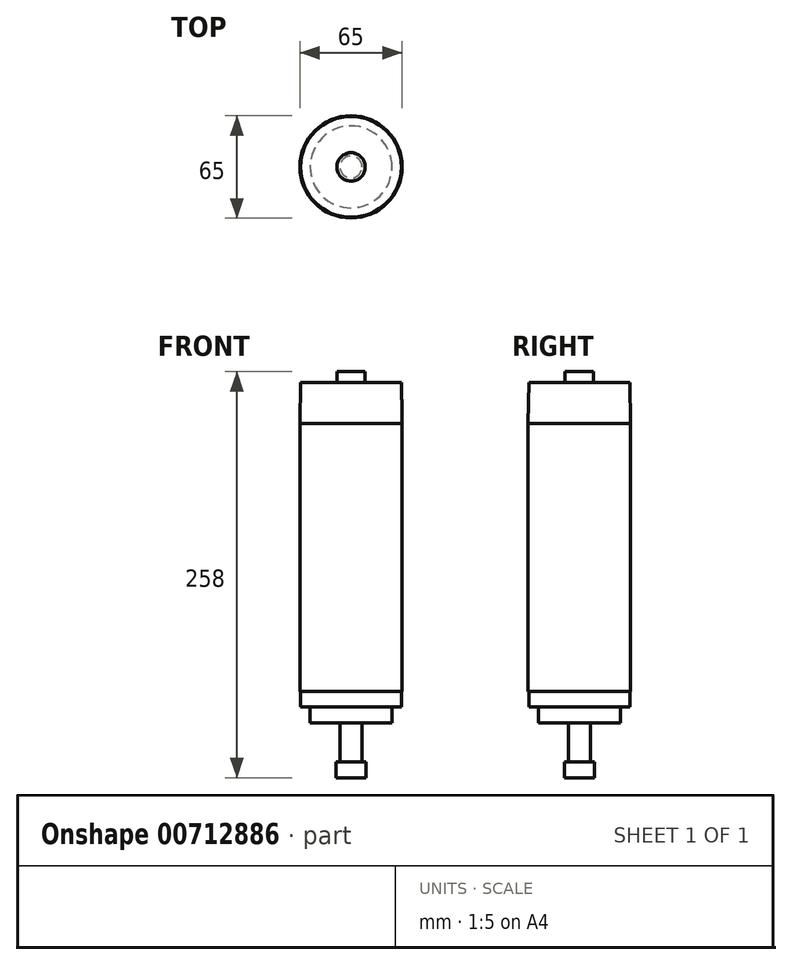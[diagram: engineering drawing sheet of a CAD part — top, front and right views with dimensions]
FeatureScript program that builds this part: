
annotation { "Feature Type Name" : "Feature", "Feature Type Description" : "" }
export const myFeature = defineFeature(function(context is Context, id is Id, definition is map)
    precondition{}
    {
        {
            var Q0;
            Q0=qCreatedBy(makeId("Top.planeOp"),FACE);
            var sketch = newSketch(context, id + "F0", { "sketchPlane" : qUnion([Q0])});
            skCircle(sketch, "E0", {"center": v(0, 0) * mm, "radius": 32.5 * mm});
            skSolve(sketch);
        }
        {
            var Q0;
            Q0 = qSketchRegion(id + "F0", true);
            extrude(context, id + "F1", {"entities" : qUnion([Q0]), "depth" : (170 + 26) * mm, "offsetDistance" : 25 * mm});
        }
        {
            var Q0;
            Q0=makeQuery(id+"F1.opExtrude","CAP_EDGE",EDGE,{"disambiguationData":[OSD([sQuery(id+"F0.wireOp",EDGE,"E0")])],"isStart":false});
            chamfer(context, id + "F2", {"entities" : qUnion([Q0]), "chamferType" : ChamferType.TWO_OFFSETS, "width1" : 26 * mm, "oppositeDirection" : true, "width2" : 0.5 * mm, "tangentPropagation" : true});
        }
        {
            var Q0;
            Q0=makeQuery(id+"F1.opExtrude","CAP_FACE",FACE,{"disambiguationData":[OSD([sQuery(id+"F0.wireOp",EDGE,"E0")])],"isStart":true});
            var sketch = newSketch(context, id + "F3", { "sketchPlane" : qUnion([Q0])});
            skCircle(sketch, "E1", {"center": v(0, 0) * mm, "radius": 32 * mm});
            skSolve(sketch);
        }
        {
            var Q0;
            Q0 = qSketchRegion(id + "F3", true);
            extrude(context, id + "F4", {"entities" : qUnion([Q0]), "operationType" : NewBodyOperationType.ADD, "depth" : 10 * mm, "offsetDistance" : 25 * mm});
        }
        {
            var Q0;
            Q0=makeQuery(id+"F4.opExtrude","CAP_FACE",FACE,{"disambiguationData":[OSD([sQuery(id+"F3.wireOp",EDGE,"E1")])],"isStart":false});
            var sketch = newSketch(context, id + "F5", { "sketchPlane" : qUnion([Q0])});
            skCircle(sketch, "E2", {"center": v(0, 0) * mm, "radius": 26 * mm});
            skSolve(sketch);
        }
        {
            var Q0;
            Q0 = qSketchRegion(id + "F5", true);
            extrude(context, id + "F6", {"entities" : qUnion([Q0]), "operationType" : NewBodyOperationType.ADD, "depth" : 10 * mm, "offsetDistance" : 25 * mm});
        }
        {
            var Q0;
            Q0=makeQuery(id+"F6.opExtrude","CAP_FACE",FACE,{"disambiguationData":[OSD([sQuery(id+"F5.wireOp",EDGE,"E2")])],"isStart":false});
            var sketch = newSketch(context, id + "F7", { "sketchPlane" : qUnion([Q0])});
            skCircle(sketch, "E3", {"center": v(0, 0) * mm, "radius": 7 * mm});
            skSolve(sketch);
        }
        {
            var Q0;
            Q0 = qSketchRegion(id + "F7", true);
            extrude(context, id + "F8", {"entities" : qUnion([Q0]), "operationType" : NewBodyOperationType.ADD, "depth" : 25 * mm, "offsetDistance" : 25 * mm});
        }
        {
            var Q0;
            Q0=makeQuery(id+"F8.opExtrude","CAP_FACE",FACE,{"disambiguationData":[OSD([sQuery(id+"F7.wireOp",EDGE,"E3")])],"isStart":false});
            var sketch = newSketch(context, id + "F9", { "sketchPlane" : qUnion([Q0])});
            skCircle(sketch, "E4", {"center": v(0, 0) * mm, "radius": 9.5 * mm});
            skSolve(sketch);
        }
        {
            var Q0;
            Q0 = qSketchRegion(id + "F9", true);
            extrude(context, id + "F10", {"entities" : qUnion([Q0]), "operationType" : NewBodyOperationType.ADD, "depth" : 10 * mm, "offsetDistance" : 25 * mm});
        }
        {
            var Q0;
            Q0=makeQuery(id+"F1.opExtrude","CAP_FACE",FACE,{"disambiguationData":[OSD([sQuery(id+"F0.wireOp",EDGE,"E0")])],"isStart":false});
            var sketch = newSketch(context, id + "F11", { "sketchPlane" : qUnion([Q0])});
            skCircle(sketch, "E5", {"center": v(0, 0) * mm, "radius": 9 * mm});
            skSolve(sketch);
        }
        {
            var Q0;
            Q0 = qSketchRegion(id + "F11", true);
            extrude(context, id + "F12", {"entities" : qUnion([Q0]), "operationType" : NewBodyOperationType.ADD, "depth" : 7 * mm, "offsetDistance" : 25 * mm});
        }
    });
